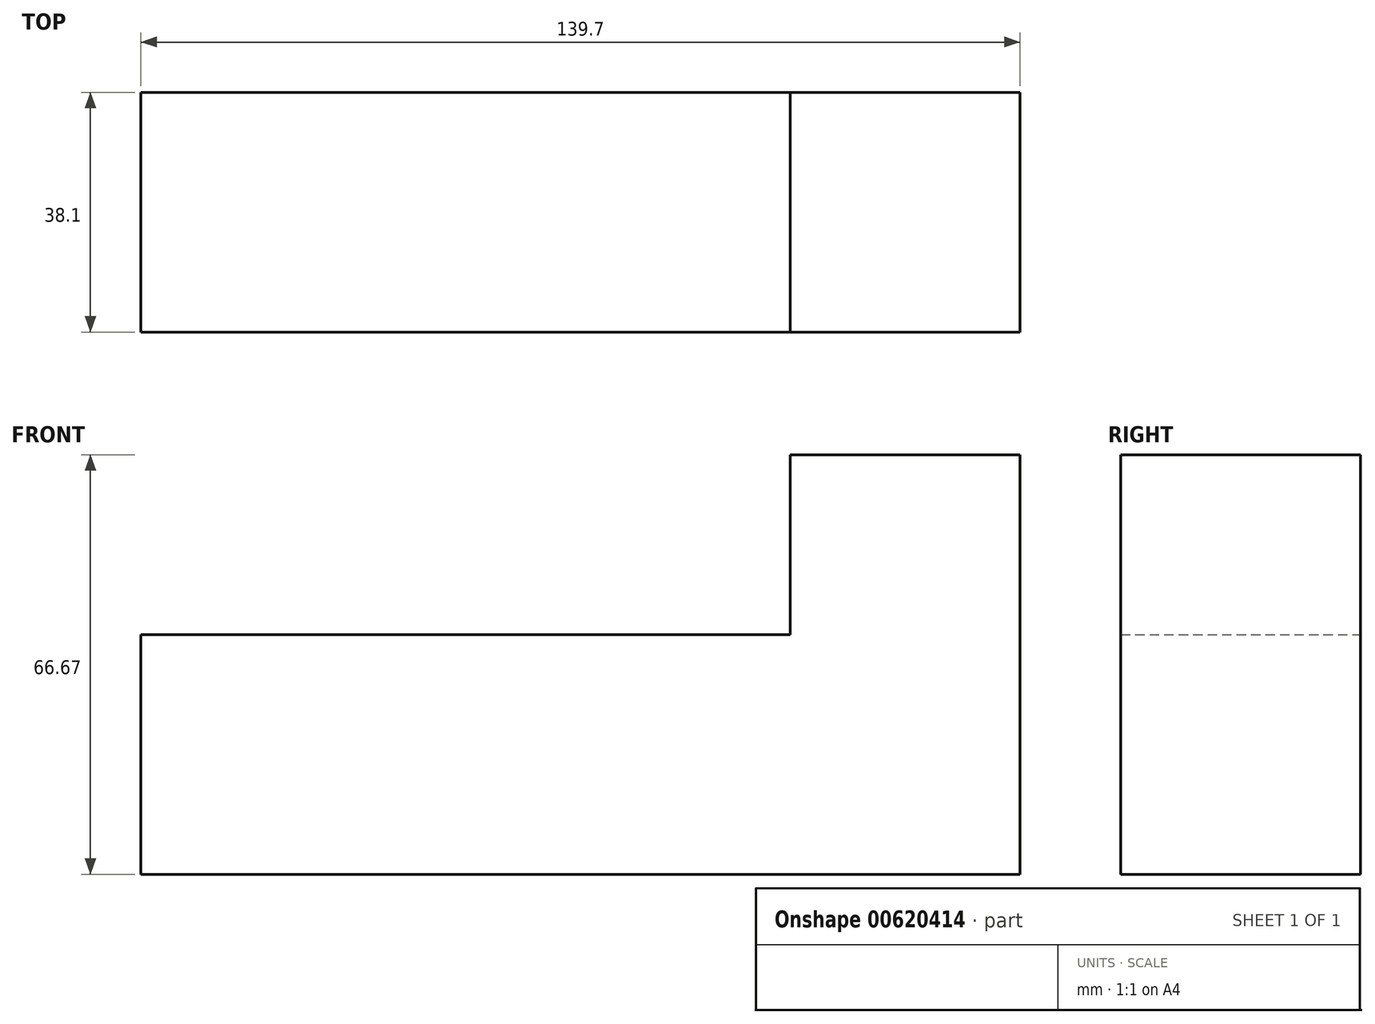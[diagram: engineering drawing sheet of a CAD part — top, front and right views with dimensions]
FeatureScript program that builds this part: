
annotation { "Feature Type Name" : "Feature", "Feature Type Description" : "" }
export const myFeature = defineFeature(function(context is Context, id is Id, definition is map)
    precondition{}
    {
        {
            var Q0;
            Q0=qCreatedBy(makeId("Front.planeOp"),FACE);
            var sketch = newSketch(context, id + "F0", { "sketchPlane" : qUnion([Q0])});
            skLineSegment(sketch, "E0", {"start": v(-9.92, -3.7) * mm, "end": v(129.78, -3.7) * mm});
            skLineSegment(sketch, "E1", {"start": v(129.78, -3.7) * mm, "end": v(129.78, 62.97) * mm});
            skLineSegment(sketch, "E2", {"start": v(129.78, 62.97) * mm, "end": v(93.27, 62.97) * mm});
            skLineSegment(sketch, "E3", {"start": v(93.27, 62.97) * mm, "end": v(93.27, 34.4) * mm});
            skLineSegment(sketch, "E4", {"start": v(93.27, 34.4) * mm, "end": v(-9.92, 34.4) * mm});
            skLineSegment(sketch, "E5", {"start": v(-9.92, 34.4) * mm, "end": v(-9.92, -3.7) * mm});
            skSolve(sketch);
        }
        {
            var Q0;
            Q0 = qSketchRegion(id + "F0", true);
            extrude(context, id + "F1", {"entities" : qUnion([Q0]), "depth" : 38.1 * mm, "offsetDistance" : 25.4 * mm});
        }
    });
